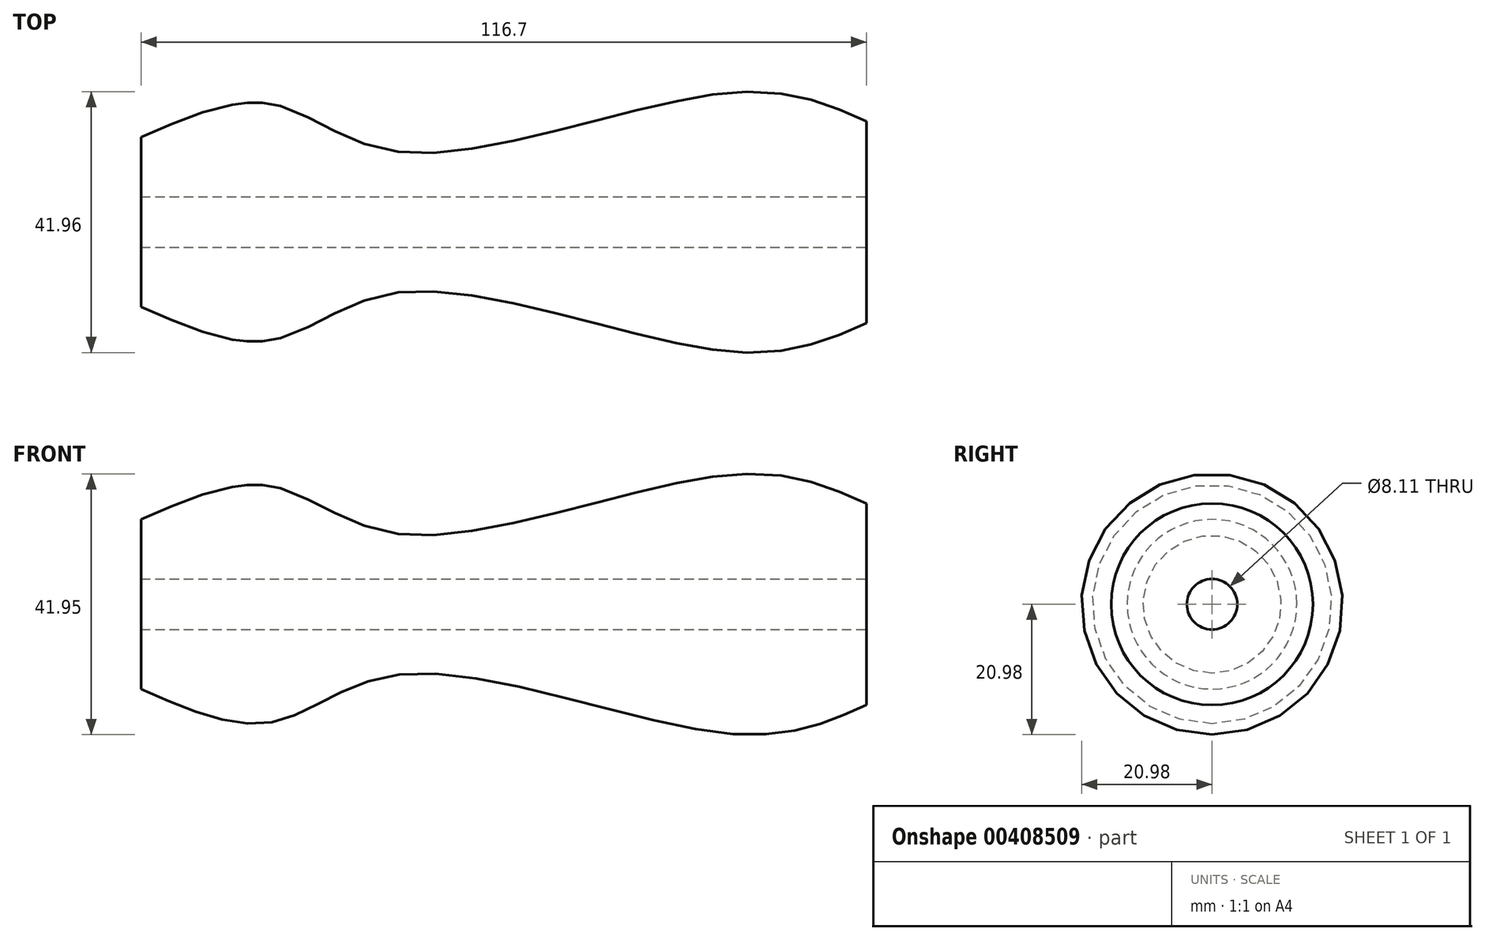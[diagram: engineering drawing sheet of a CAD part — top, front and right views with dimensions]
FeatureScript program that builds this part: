
annotation { "Feature Type Name" : "Feature", "Feature Type Description" : "" }
export const myFeature = defineFeature(function(context is Context, id is Id, definition is map)
    precondition{}
    {
        {
            var Q0;
            Q0=qCreatedBy(makeId("Front.planeOp"),FACE);
            var sketch = newSketch(context, id + "F0", { "sketchPlane" : qUnion([Q0])});
            skLineSegment(sketch, "E0", {"start": v(0, 0) * mm, "end": v(-116.7, 0) * mm});
            skLineSegment(sketch, "E1", {"start": v(-116.7, 0) * mm, "end": v(-116.7, 13.64) * mm});
            skFitSpline(sketch, "E2", {"points": [v(-116.7, 13.64) * mm, v(-95.68, 18.99) * mm, v(-74.85, 11.25) * mm, v(-21.94, 20.83) * mm, v(0, 16.22) * mm], "startDerivative": vector(101.63, 44.75) * mm, "endDerivative": vector(83.1, -36.94) * mm});
            skLineSegment(sketch, "E3", {"start": v(0, 16.22) * mm, "end": v(0, 0) * mm});
            skLineSegment(sketch, "E4", {"start": v(-116.7, 4.06) * mm, "end": v(0, 4.06) * mm});
            skSolve(sketch);
        }
        {
            var Q0;
            {var subQ0=sQuery(id+"F0.wireOp",EDGE,"E2");Q0=makeQuery(id+"F0.imprint","IMPRINT",FACE,{"disambiguationData":[TD([[makeQuery(id+"F0.imprint","IMPRINT",EDGE,{"derivedFrom":subQ0}),-1.0]])]});}
            var Q1;
            Q1=sQuery(id+"F0.wireOp",EDGE,"E0");
            revolve(context, id + "F1", {"entities" : qUnion([Q0]), "axis" : qUnion([Q1]), "revolveType" : RevolveType.FULL});
        }
    });
